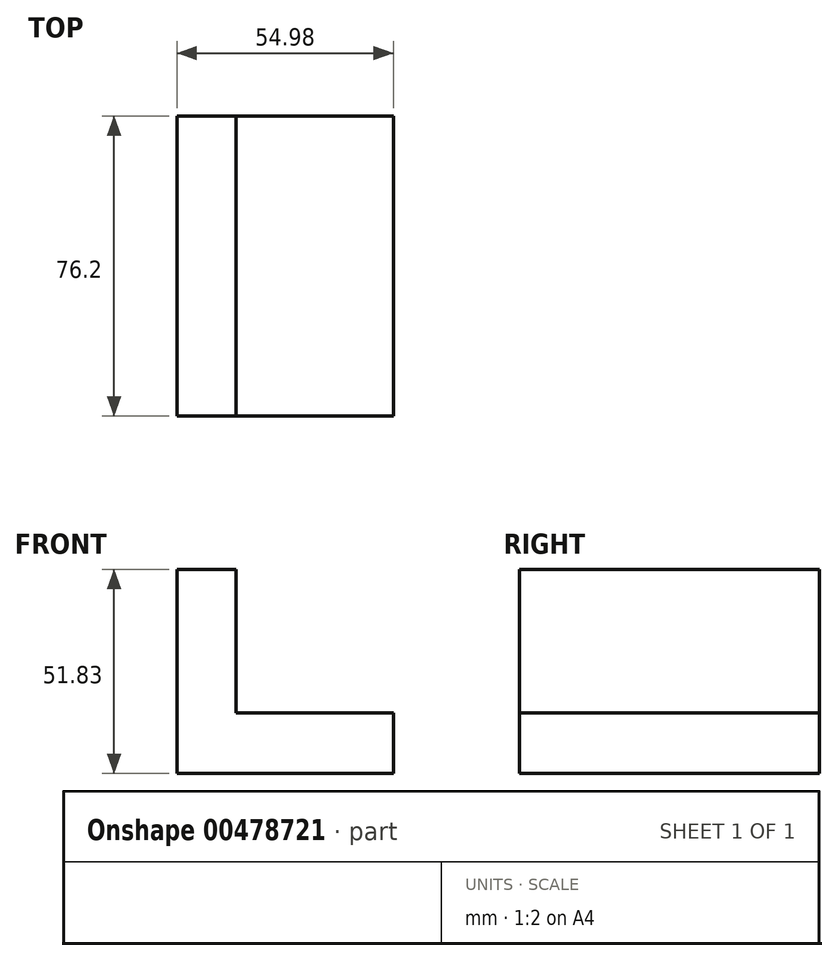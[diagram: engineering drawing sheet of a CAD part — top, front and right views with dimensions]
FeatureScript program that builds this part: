
annotation { "Feature Type Name" : "Feature", "Feature Type Description" : "" }
export const myFeature = defineFeature(function(context is Context, id is Id, definition is map)
    precondition{}
    {
        {
            var Q0;
            Q0=qCreatedBy(makeId("Front.planeOp"),FACE);
            var sketch = newSketch(context, id + "F0", { "sketchPlane" : qUnion([Q0])});
            skLineSegment(sketch, "E0", {"start": v(0, 0) * mm, "end": v(0, 51.83) * mm});
            skLineSegment(sketch, "E1", {"start": v(0, 51.83) * mm, "end": v(14.98, 51.83) * mm});
            skLineSegment(sketch, "E2", {"start": v(14.98, 51.83) * mm, "end": v(14.98, 15.37) * mm});
            skLineSegment(sketch, "E3", {"start": v(14.98, 15.37) * mm, "end": v(54.98, 15.37) * mm});
            skLineSegment(sketch, "E4", {"start": v(54.98, 15.37) * mm, "end": v(54.98, 0) * mm});
            skLineSegment(sketch, "E5", {"start": v(54.98, 0) * mm, "end": v(0, 0) * mm});
            skSolve(sketch);
        }
        {
            var Q0;
            Q0=makeQuery(id+"F0.imprint","IMPRINT",FACE,{"disambiguationData":[TD([[makeQuery(id+"F0.imprint","IMPRINT",EDGE,{"derivedFrom":sQuery(id+"F0.wireOp",EDGE,"E0")}),-1.0]])]});
            extrude(context, id + "F1", {"entities" : qUnion([Q0]), "depth" : 76.2 * mm});
        }
    });
